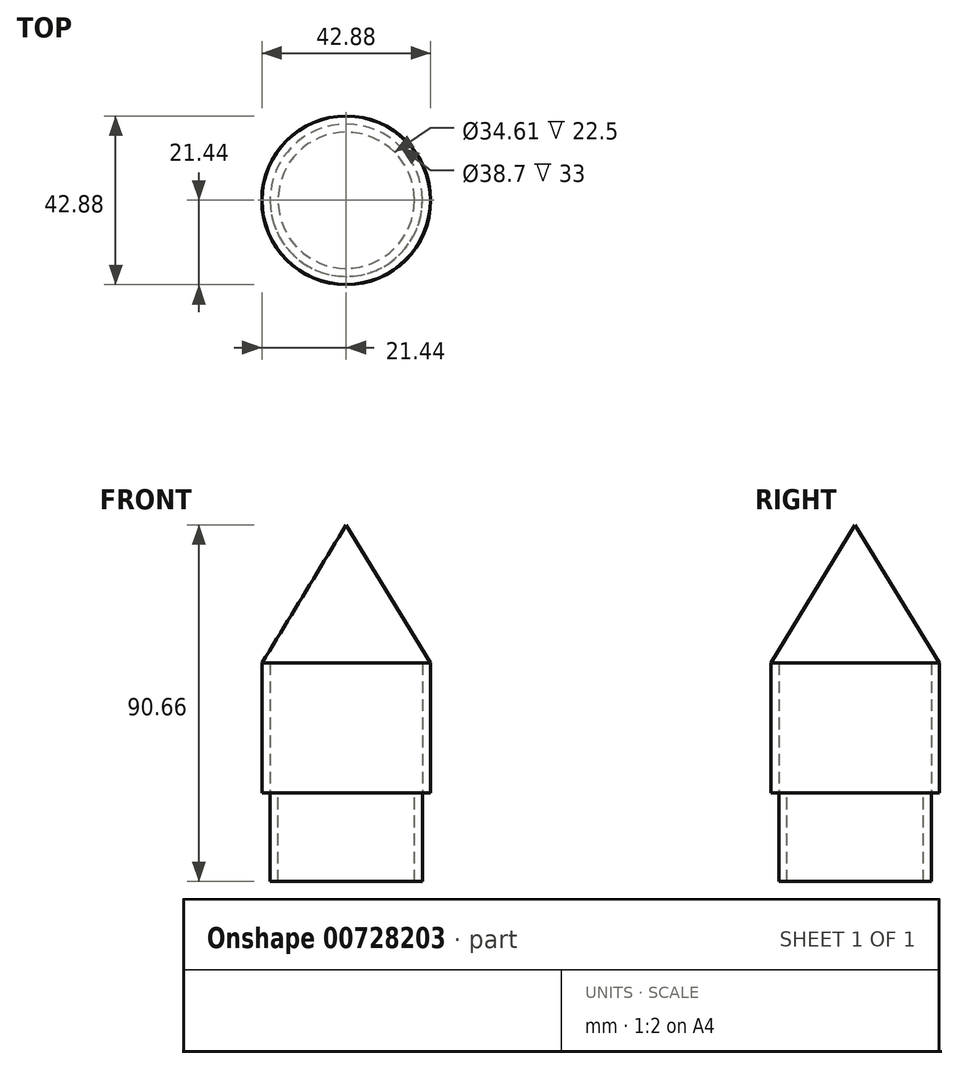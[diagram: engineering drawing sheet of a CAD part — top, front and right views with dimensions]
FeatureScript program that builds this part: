
annotation { "Feature Type Name" : "Feature", "Feature Type Description" : "" }
export const myFeature = defineFeature(function(context is Context, id is Id, definition is map)
    precondition{}
    {
        {
            var Q0;
            Q0=qCreatedBy(makeId("Top.planeOp"),FACE);
            var sketch = newSketch(context, id + "F0", { "sketchPlane" : qUnion([Q0])});
            skCircle(sketch, "E0", {"center": v(0, 0) * mm, "radius": 21.43 * mm});
            skSolve(sketch);
        }
        {
            var Q0;
            Q0=makeQuery(id+"F0.imprint","IMPRINT",FACE,{"disambiguationData":[TD([[makeQuery(id+"F0.imprint","IMPRINT",EDGE,{"derivedFrom":sQuery(id+"F0.wireOp",EDGE,"E0")}),1.0]])]});
            extrude(context, id + "F1", {"entities" : qUnion([Q0]), "depth" : 33 * mm, "offsetDistance" : 25 * mm});
        }
        {
            var Q0;
            Q0=qCreatedBy(makeId("Top.planeOp"),FACE);
            var sketch = newSketch(context, id + "F2", { "sketchPlane" : qUnion([Q0])});
            skCircle(sketch, "E1", {"center": v(0, 0) * mm, "radius": 19.35 * mm});
            skSolve(sketch);
        }
        {
            var Q0;
            Q0=sQuery(id+"F2.wireOp",VERTEX,"E1.center");
            var Q1;
            Q1=makeQuery(id+"F1.opExtrude","SWEPT_BODY",BODY,{"disambiguationData":[OSD([sQuery(id+"F0.wireOp",EDGE,"E0")])]});
            hole(context, id + "F3", {"style" : HoleStyle.SIMPLE, "endStyle" : HoleEndStyle.THROUGH, "oppositeDirection" : true, "holeDiameter" : 38.7 * mm, "majorDiameter" : 5 * mm, "isTappedThrough" : true, "tappedDepth" : 12 * mm, "tapClearance" : 3, "locations" : qUnion([Q0]), "scope" : qUnion([Q1])});
        }
        {
            var Q0;
            Q0=qCreatedBy(makeId("Front.planeOp"),FACE);
            var sketch = newSketch(context, id + "F4", { "sketchPlane" : qUnion([Q0])});
            skLineSegment(sketch, "E2", {"start": v(0, 0) * mm, "end": v(0, 32.6) * mm});
            skSolve(sketch);
        }
        {
            var Q0;
            Q0=qCreatedBy(makeId("Top.planeOp"),FACE);
            var sketch = newSketch(context, id + "F5", { "sketchPlane" : qUnion([Q0])});
            skCircle(sketch, "E3", {"center": v(0, 0) * mm, "radius": 19.35 * mm});
            skCircle(sketch, "E4", {"center": v(0, 0) * mm, "radius": 17.3 * mm});
            skSolve(sketch);
        }
        {
            var Q0;
            Q0=makeQuery(id+"F5.imprint","IMPRINT",FACE,{"disambiguationData":[TD([[makeQuery(id+"F5.imprint","IMPRINT",EDGE,{"derivedFrom":sQuery(id+"F5.wireOp",EDGE,"E3")}),1.0]])]});
            extrude(context, id + "F6", {"entities" : qUnion([Q0]), "oppositeDirection" : true, "depth" : 22.5 * mm, "offsetDistance" : 25 * mm});
        }
        {
            var Q0;
            Q0=qCreatedBy(makeId("Front.planeOp"),FACE);
            var sketch = newSketch(context, id + "F7", { "sketchPlane" : qUnion([Q0])});
            skLineSegment(sketch, "E5", {"start": v(-21.38, 33.02) * mm, "end": v(0, 33.02) * mm});
            skLineSegment(sketch, "E6", {"start": v(0, 33.02) * mm, "end": v(0, 68.16) * mm});
            skLineSegment(sketch, "E7", {"start": v(0, 68.16) * mm, "end": v(-21.38, 33.02) * mm});
            skSolve(sketch);
        }
        {
            var Q0;
            Q0=makeQuery(id+"F7.imprint","IMPRINT",FACE,{"disambiguationData":[TD([[makeQuery(id+"F7.imprint","IMPRINT",EDGE,{"derivedFrom":sQuery(id+"F7.wireOp",EDGE,"E5")}),1.0]])]});
            var Q1;
            Q1=sQuery(id+"F4.wireOp",EDGE,"E2");
            revolve(context, id + "F8", {"surfaceOperationType" : NewSurfaceOperationType.NEW, "entities" : qUnion([Q0]), "axis" : qUnion([Q1]), "revolveType" : RevolveType.FULL});
        }
        {
            var Q0;
            Q0=makeQuery(id+"F1.opExtrude","CAP_FACE",FACE,{"disambiguationData":[OSD([sQuery(id+"F0.wireOp",EDGE,"E0")])],"isStart":false});
            var sketch = newSketch(context, id + "F9", { "sketchPlane" : qUnion([Q0])});
            skCircle(sketch, "E8", {"center": v(0, 0) * mm, "radius": 21.36 * mm});
            skCircle(sketch, "E9", {"center": v(0, 0) * mm, "radius": 30.15 * mm});
            skSolve(sketch);
        }
        {
            var Q0;
            Q0=makeQuery(id+"F9.imprint","IMPRINT",FACE,{"disambiguationData":[TD([[makeQuery(id+"F9.imprint","IMPRINT",EDGE,{"derivedFrom":sQuery(id+"F9.wireOp",EDGE,"E9")}),1.0]])]});
            extrude(context, id + "F10", {"entities" : qUnion([Q0]), "operationType" : NewBodyOperationType.REMOVE, "oppositeDirection" : true, "depth" : 71.5 * mm, "offsetDistance" : 25 * mm});
        }
    });
